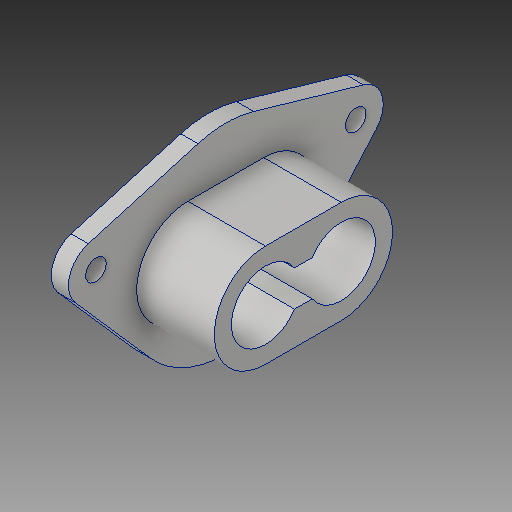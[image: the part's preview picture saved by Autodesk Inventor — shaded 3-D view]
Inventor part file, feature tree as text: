
AUTODESK INVENTOR PART (.ipt)
format: ipt  version: 2019 (Build 230136000, 136)  size: 159,232 bytes
history: native  units: in
note: dims shown in document units (in); Inventor stores cm internally (conversion verified against a paired STEP export)
features: other x3, sketch x2
ambient origin geometry x8: Origin, YZ Plane, XZ Plane, XY Plane, X Axis, Y Axis, Z Axis, Center Point
bodies: Solid1 (feature_tree)
feature tree (5):
  other  "MotorFixedPositionMountInvertedDrive.ipt"
  other  "Solid1::MotorFixedPositionMountInvertedDrive.ipt"
  other  "TaggingFeature1"
  sketch  "Sketch1"  dims[d0=0.3937in]
  sketch  "Sketch6"
